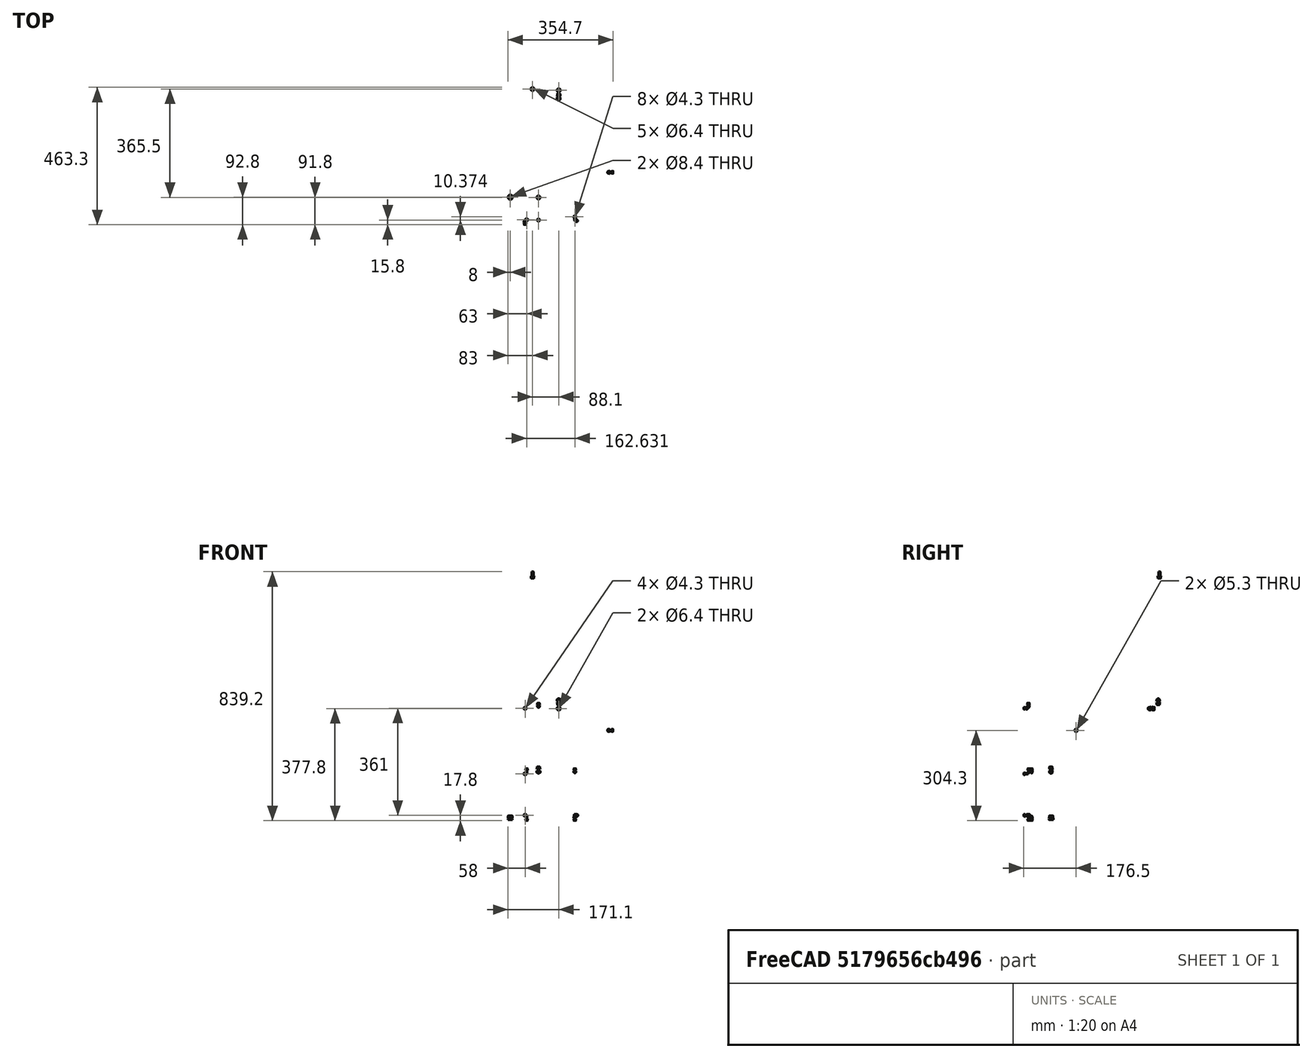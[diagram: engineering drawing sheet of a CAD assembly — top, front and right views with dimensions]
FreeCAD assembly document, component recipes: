
FREECAD ASSEMBLY — COMPONENT RECIPES ("OCT-FRAME-A")

This assembly document has 87 components, labeled P0..P86 below (a component is one placed body or linked part). 0 of them carry a construction recipe — the FreeCAD feature program that regenerates the part from scratch, quoted from this document or its linked companion documents; the rest are supplied as boundary geometry only. No exploded tour is included for this assembly.
COMPONENT P0 — geometry summary ("OCT-FRPLB-AA"; no construction recipe available for this part):
  bounding box: 422.0 x 422.0 x 3.0 mm
  tessellated surface: 3,756 triangles
  volume: 441062 mm^3 (83% of its bounding box)
  symmetry: 2-fold rotationally symmetric about the x axis; 2-fold rotationally symmetric about the y axis; 4-fold rotationally symmetric about the z axis; mirror-symmetric across its x mid-plane, y mid-plane, z mid-plane
COMPONENT P1 — geometry summary ("OCT-FRPLC-AA"; no construction recipe available for this part):
  bounding box: 422.0 x 422.0 x 3.0 mm
  tessellated surface: 8,208 triangles
  volume: 428125 mm^3 (80% of its bounding box)
COMPONENT P2 — geometry summary ("OCT-CPBRC-BA"; no construction recipe available for this part):
  bounding box: 170.0 x 20.0 x 20.0 mm
  tessellated surface: 804 triangles
  volume: 6888 mm^3 (10% of its bounding box)
  symmetry: mirror-symmetric across its x mid-plane
COMPONENT P3 — geometry summary ("OCT-LFPNL-AB"; no construction recipe available for this part):
  bounding box: 140.0 x 125.0 x 125.0 mm
  tessellated surface: 700 triangles
  volume: 48735 mm^3 (2% of its bounding box)
  symmetry: 2-fold rotationally symmetric about the z axis; mirror-symmetric across its z mid-plane
COMPONENT P4 — geometry summary ("OCT-LFPNL-AB"; no construction recipe available for this part):
  bounding box: 174.8 x 140.0 x 2.0 mm
  tessellated surface: 700 triangles
  volume: 48735 mm^3 (100% of its bounding box)
  symmetry: 2-fold rotationally symmetric about the x axis; 2-fold rotationally symmetric about the y axis; 2-fold rotationally symmetric about the z axis; mirror-symmetric across its x mid-plane, z mid-plane
COMPONENT P5 — geometry summary ("OCT-LFPNL-AB"; no construction recipe available for this part):
  bounding box: 140.0 x 125.0 x 125.0 mm
  tessellated surface: 700 triangles
  volume: 48735 mm^3 (2% of its bounding box)
  symmetry: 2-fold rotationally symmetric about the z axis; mirror-symmetric across its z mid-plane
COMPONENT P6 — geometry summary ("OCT-LFPNL-AB"; no construction recipe available for this part):
  bounding box: 140.0 x 125.0 x 125.0 mm
  tessellated surface: 700 triangles
  volume: 48735 mm^3 (2% of its bounding box)
  symmetry: 2-fold rotationally symmetric about the z axis; mirror-symmetric across its z mid-plane
COMPONENT P7 — geometry summary ("OCT-LFPNL-AB"; no construction recipe available for this part):
  bounding box: 174.8 x 140.0 x 2.0 mm
  tessellated surface: 700 triangles
  volume: 48735 mm^3 (100% of its bounding box)
  symmetry: 2-fold rotationally symmetric about the x axis; 2-fold rotationally symmetric about the y axis; 2-fold rotationally symmetric about the z axis; mirror-symmetric across its x mid-plane, z mid-plane
COMPONENT P8 — geometry summary ("OCT-LFPNL-AB"; no construction recipe available for this part):
  bounding box: 140.0 x 125.0 x 125.0 mm
  tessellated surface: 700 triangles
  volume: 48735 mm^3 (2% of its bounding box)
  symmetry: 2-fold rotationally symmetric about the z axis; mirror-symmetric across its z mid-plane
COMPONENT P9 — geometry summary ("OCT-LFPNL-BA"; no construction recipe available for this part):
  bounding box: 174.8 x 140.0 x 2.0 mm
  tessellated surface: 1,360 triangles
  volume: 29007 mm^3 (59% of its bounding box)
  symmetry: 2-fold rotationally symmetric about the x axis; 2-fold rotationally symmetric about the y axis; mirror-symmetric across its x mid-plane, y mid-plane
COMPONENT P10 — geometry summary ("OCT-LFPNL-CA"; no construction recipe available for this part):
  bounding box: 174.8 x 140.0 x 2.0 mm
  tessellated surface: 1,664 triangles
  volume: 27031 mm^3 (55% of its bounding box)
  symmetry: mirror-symmetric across its y mid-plane
COMPONENT P11 — geometry summary ("OCT-UFPNL-BB"; no construction recipe available for this part):
  bounding box: 241.0 x 174.8 x 1.5 mm
  tessellated surface: 1,580 triangles
  volume: 62827 mm^3 (99% of its bounding box)
  symmetry: 2-fold rotationally symmetric about the x axis; 2-fold rotationally symmetric about the y axis; 2-fold rotationally symmetric about the z axis; mirror-symmetric across its x mid-plane, y mid-plane, z mid-plane
COMPONENT P12 — geometry summary ("OCT-UFPNL-CB"; no construction recipe available for this part):
  bounding box: 241.0 x 174.8 x 1.5 mm
  tessellated surface: 1,324 triangles
  volume: 62936 mm^3 (100% of its bounding box)
  symmetry: 2-fold rotationally symmetric about the x axis; 2-fold rotationally symmetric about the y axis; 2-fold rotationally symmetric about the z axis; mirror-symmetric across its x mid-plane, y mid-plane, z mid-plane
COMPONENT P13 — geometry summary ("OCT-UFPNL-CB"; no construction recipe available for this part):
  bounding box: 241.0 x 174.8 x 1.5 mm
  tessellated surface: 1,324 triangles
  volume: 62936 mm^3 (100% of its bounding box)
  symmetry: 2-fold rotationally symmetric about the x axis; 2-fold rotationally symmetric about the y axis; 2-fold rotationally symmetric about the z axis; mirror-symmetric across its x mid-plane, y mid-plane, z mid-plane
COMPONENT P14 — geometry summary ("WDS4213-601"; no construction recipe available for this part):
  bounding box: 110.0 x 79.4 x 15.4 mm
  tessellated surface: 75,042 triangles
  volume: 34211 mm^3 (25% of its bounding box)
  symmetry: mirror-symmetric across its y mid-plane
COMPONENT P15 — geometry summary ("WDS4213-601"; no construction recipe available for this part):
  bounding box: 110.0 x 79.4 x 15.4 mm
  tessellated surface: 75,042 triangles
  volume: 34211 mm^3 (25% of its bounding box)
  symmetry: mirror-symmetric across its y mid-plane
COMPONENT P16 — geometry summary ("WDS673-82225"; no construction recipe available for this part):
  bounding box: 45.3 x 40.0 x 40.0 mm
  tessellated surface: 20,496 triangles
  volume: 12551 mm^3 (17% of its bounding box)
  symmetry: revolution-symmetric about the z axis through its bounding-box center; mirror-symmetric across its x mid-plane, y mid-plane
COMPONENT P17 — geometry summary ("WDS673-82225"; no construction recipe available for this part):
  bounding box: 45.3 x 40.0 x 40.0 mm
  tessellated surface: 20,496 triangles
  volume: 12551 mm^3 (17% of its bounding box)
  symmetry: revolution-symmetric about the z axis through its bounding-box center; mirror-symmetric across its x mid-plane, y mid-plane
COMPONENT P18 — geometry summary ("WDS673-82225"; no construction recipe available for this part):
  bounding box: 45.3 x 40.0 x 40.0 mm
  tessellated surface: 20,496 triangles
  volume: 12551 mm^3 (17% of its bounding box)
  symmetry: revolution-symmetric about the z axis through its bounding-box center; mirror-symmetric across its x mid-plane, y mid-plane
COMPONENT P19 — geometry summary ("WDS673-82225"; no construction recipe available for this part):
  bounding box: 45.3 x 40.0 x 40.0 mm
  tessellated surface: 20,496 triangles
  volume: 12551 mm^3 (17% of its bounding box)
  symmetry: revolution-symmetric about the z axis through its bounding-box center; mirror-symmetric across its x mid-plane, y mid-plane
COMPONENT P20 — geometry summary ("WDS8520-251"; no construction recipe available for this part):
  bounding box: 113.0 x 50.0 x 20.0 mm
  tessellated surface: 14,568 triangles
  volume: 33965 mm^3 (30% of its bounding box)
  symmetry: mirror-symmetric across its x mid-plane, y mid-plane
COMPONENT P21 — geometry summary ("637DSS"; no construction recipe available for this part):
  bounding box: 102.0 x 52.0 x 1.2 mm
  tessellated surface: 1,244 triangles
  volume: 6170 mm^3 (97% of its bounding box)
  symmetry: 2-fold rotationally symmetric about the x axis; 2-fold rotationally symmetric about the y axis; mirror-symmetric across its y mid-plane, z mid-plane
COMPONENT P22 — geometry summary ("637DSS"; no construction recipe available for this part):
  bounding box: 102.0 x 52.0 x 1.2 mm
  tessellated surface: 1,244 triangles
  volume: 6170 mm^3 (97% of its bounding box)
  symmetry: 2-fold rotationally symmetric about the x axis; 2-fold rotationally symmetric about the y axis; mirror-symmetric across its y mid-plane, z mid-plane
COMPONENT P23 — geometry summary ("baseplate block fasteners"; no construction recipe available for this part):
  bounding box: 411.0 x 149.0 x 16.0 mm
  tessellated surface: 8,512 triangles
  volume: 1289 mm^3 (0% of its bounding box)
  symmetry: 2-fold rotationally symmetric about the z axis; mirror-symmetric across its x mid-plane, y mid-plane
COMPONENT P24 — geometry summary ("baseplate bracket fasteners"; no construction recipe available for this part):
  bounding box: 412.4 x 394.3 x 16.0 mm
  tessellated surface: 83,040 triangles
  volume: 11254 mm^3 (0% of its bounding box)
  symmetry: 2-fold rotationally symmetric about the x axis; 2-fold rotationally symmetric about the y axis; 2-fold rotationally symmetric about the z axis; mirror-symmetric across its x mid-plane, y mid-plane, z mid-plane
COMPONENT P25 — geometry summary ("OCT-CHBRA-AC"; no construction recipe available for this part):
  bounding box: 80.0 x 25.0 x 25.0 mm
  tessellated surface: 600 triangles
  volume: 11180 mm^3 (22% of its bounding box)
  symmetry: mirror-symmetric across its x mid-plane
COMPONENT P26 — geometry summary ("OCT-CHBRA-AC"; no construction recipe available for this part):
  bounding box: 74.2 x 74.2 x 25.0 mm
  tessellated surface: 600 triangles
  volume: 11180 mm^3 (8% of its bounding box)
COMPONENT P27 — geometry summary ("OCT-CHBRA-AC"; no construction recipe available for this part):
  bounding box: 80.0 x 25.0 x 25.0 mm
  tessellated surface: 600 triangles
  volume: 11180 mm^3 (22% of its bounding box)
  symmetry: mirror-symmetric across its x mid-plane
COMPONENT P28 — geometry summary ("OCT-CHBRA-AC"; no construction recipe available for this part):
  bounding box: 74.2 x 74.2 x 25.0 mm
  tessellated surface: 600 triangles
  volume: 11180 mm^3 (8% of its bounding box)
COMPONENT P29 — geometry summary ("OCT-CHBRA-AC"; no construction recipe available for this part):
  bounding box: 80.0 x 25.0 x 25.0 mm
  tessellated surface: 600 triangles
  volume: 11180 mm^3 (22% of its bounding box)
  symmetry: mirror-symmetric across its x mid-plane
COMPONENT P30 — geometry summary ("OCT-CHBRA-AC"; no construction recipe available for this part):
  bounding box: 74.2 x 74.2 x 25.0 mm
  tessellated surface: 600 triangles
  volume: 11180 mm^3 (8% of its bounding box)
COMPONENT P31 — geometry summary ("OCT-CHBRA-AC"; no construction recipe available for this part):
  bounding box: 80.0 x 25.0 x 25.0 mm
  tessellated surface: 600 triangles
  volume: 11180 mm^3 (22% of its bounding box)
  symmetry: mirror-symmetric across its x mid-plane
COMPONENT P32 — geometry summary ("OCT-CHBRA-AC"; no construction recipe available for this part):
  bounding box: 74.2 x 74.2 x 25.0 mm
  tessellated surface: 600 triangles
  volume: 11180 mm^3 (8% of its bounding box)
COMPONENT P33 — geometry summary ("OCT-LBRAC-AA"; no construction recipe available for this part):
  bounding box: 123.3 x 123.3 x 20.0 mm
  tessellated surface: 620 triangles
  volume: 9368 mm^3 (3% of its bounding box)
COMPONENT P34 — geometry summary ("OCT-LBRAC-AA"; no construction recipe available for this part):
  bounding box: 170.0 x 20.0 x 20.0 mm
  tessellated surface: 620 triangles
  volume: 9368 mm^3 (14% of its bounding box)
  symmetry: mirror-symmetric across its y mid-plane
COMPONENT P35 — geometry summary ("OCT-LBRAC-AA"; no construction recipe available for this part):
  bounding box: 123.3 x 123.3 x 20.0 mm
  tessellated surface: 620 triangles
  volume: 9368 mm^3 (3% of its bounding box)
COMPONENT P36 — geometry summary ("OCT-LBRAC-AA"; no construction recipe available for this part):
  bounding box: 123.3 x 123.3 x 20.0 mm
  tessellated surface: 620 triangles
  volume: 9368 mm^3 (3% of its bounding box)
COMPONENT P37 — geometry summary ("OCT-LBRAC-AA"; no construction recipe available for this part):
  bounding box: 170.0 x 20.0 x 20.0 mm
  tessellated surface: 620 triangles
  volume: 9368 mm^3 (14% of its bounding box)
  symmetry: mirror-symmetric across its y mid-plane
COMPONENT P38 — geometry summary ("OCT-LBRAC-AA"; no construction recipe available for this part):
  bounding box: 123.3 x 123.3 x 20.0 mm
  tessellated surface: 620 triangles
  volume: 9368 mm^3 (3% of its bounding box)
COMPONENT P39 — geometry summary ("OCT-UBRAC-AA"; no construction recipe available for this part):
  bounding box: 123.3 x 123.3 x 40.0 mm
  tessellated surface: 916 triangles
  volume: 14427 mm^3 (2% of its bounding box)
COMPONENT P40 — geometry summary ("OCT-UBRAC-AA"; no construction recipe available for this part):
  bounding box: 170.0 x 40.0 x 20.0 mm
  tessellated surface: 916 triangles
  volume: 14427 mm^3 (11% of its bounding box)
  symmetry: mirror-symmetric across its y mid-plane
COMPONENT P41 — geometry summary ("OCT-UBRAC-AA"; no construction recipe available for this part):
  bounding box: 123.3 x 123.3 x 40.0 mm
  tessellated surface: 916 triangles
  volume: 14427 mm^3 (2% of its bounding box)
COMPONENT P42 — geometry summary ("OCT-UBRAC-AA"; no construction recipe available for this part):
  bounding box: 123.3 x 123.3 x 40.0 mm
  tessellated surface: 916 triangles
  volume: 14427 mm^3 (2% of its bounding box)
COMPONENT P43 — geometry summary ("OCT-UBRAC-AA"; no construction recipe available for this part):
  bounding box: 170.0 x 40.0 x 20.0 mm
  tessellated surface: 916 triangles
  volume: 14427 mm^3 (11% of its bounding box)
  symmetry: mirror-symmetric across its y mid-plane
COMPONENT P44 — geometry summary ("OCT-UBRAC-AA"; no construction recipe available for this part):
  bounding box: 123.3 x 123.3 x 40.0 mm
  tessellated surface: 916 triangles
  volume: 14427 mm^3 (2% of its bounding box)
COMPONENT P45 — geometry summary ("chamber brace fasteners"; no construction recipe available for this part):
  bounding box: 264.0 x 264.0 x 22.0 mm
  tessellated surface: 85,888 triangles
  volume: 23040 mm^3 (2% of its bounding box)
  symmetry: 2-fold rotationally symmetric about the x axis; 2-fold rotationally symmetric about the y axis; 4-fold rotationally symmetric about the z axis; mirror-symmetric across its x mid-plane, y mid-plane, z mid-plane
COMPONENT P46 — geometry summary ("OCT-CPBRC-AA"; no construction recipe available for this part):
  bounding box: 170.0 x 20.0 x 20.0 mm
  tessellated surface: 620 triangles
  volume: 9369 mm^3 (14% of its bounding box)
COMPONENT P47 — geometry summary ("OCT-CPBRC-AA"; no construction recipe available for this part):
  bounding box: 123.3 x 123.3 x 20.0 mm
  tessellated surface: 620 triangles
  volume: 9369 mm^3 (3% of its bounding box)
COMPONENT P48 — geometry summary ("OCT-CPBRC-AA"; no construction recipe available for this part):
  bounding box: 170.0 x 20.0 x 20.0 mm
  tessellated surface: 620 triangles
  volume: 9369 mm^3 (14% of its bounding box)
COMPONENT P49 — geometry summary ("OCT-CPBRC-AA"; no construction recipe available for this part):
  bounding box: 123.3 x 123.3 x 20.0 mm
  tessellated surface: 620 triangles
  volume: 9369 mm^3 (3% of its bounding box)
COMPONENT P50 — geometry summary ("OCT-CPBRC-AA"; no construction recipe available for this part):
  bounding box: 123.3 x 123.3 x 20.0 mm
  tessellated surface: 620 triangles
  volume: 9369 mm^3 (3% of its bounding box)
COMPONENT P51 — geometry summary ("OCT-CPBRC-AA"; no construction recipe available for this part):
  bounding box: 170.0 x 20.0 x 20.0 mm
  tessellated surface: 620 triangles
  volume: 9369 mm^3 (14% of its bounding box)
COMPONENT P52 — geometry summary ("OCT-CPBRC-AA"; no construction recipe available for this part):
  bounding box: 123.3 x 123.3 x 20.0 mm
  tessellated surface: 620 triangles
  volume: 9369 mm^3 (3% of its bounding box)
COMPONENT P53 — geometry summary ("foot fasteners"; no construction recipe available for this part):
  bounding box: 266.0 x 266.0 x 13.0 mm
  tessellated surface: 13,280 triangles
  volume: 4860 mm^3 (1% of its bounding box)
  symmetry: 2-fold rotationally symmetric about the x axis; 2-fold rotationally symmetric about the y axis; 4-fold rotationally symmetric about the z axis; mirror-symmetric across its x mid-plane, y mid-plane, z mid-plane
COMPONENT P54 — geometry summary ("hinge lower fastener set"; no construction recipe available for this part):
  bounding box: 22.0 x 12.0 x 12.0 mm
  tessellated surface: 5,368 triangles
  volume: 1440 mm^3 (45% of its bounding box)
  symmetry: 6-fold rotationally symmetric about the y axis; mirror-symmetric across its x mid-plane, z mid-plane
COMPONENT P55 — geometry summary ("hinge lower fastener set"; no construction recipe available for this part):
  bounding box: 22.0 x 12.0 x 12.0 mm
  tessellated surface: 5,368 triangles
  volume: 1440 mm^3 (45% of its bounding box)
  symmetry: 6-fold rotationally symmetric about the y axis; mirror-symmetric across its x mid-plane, z mid-plane
COMPONENT P56 — geometry summary ("hinge lower fastener set"; no construction recipe available for this part):
  bounding box: 22.0 x 12.0 x 12.0 mm
  tessellated surface: 5,368 triangles
  volume: 1440 mm^3 (45% of its bounding box)
  symmetry: 6-fold rotationally symmetric about the y axis; mirror-symmetric across its x mid-plane, z mid-plane
COMPONENT P57 — geometry summary ("hinge lower fastener set"; no construction recipe available for this part):
  bounding box: 22.0 x 12.0 x 12.0 mm
  tessellated surface: 5,368 triangles
  volume: 1440 mm^3 (45% of its bounding box)
  symmetry: 6-fold rotationally symmetric about the y axis; mirror-symmetric across its x mid-plane, z mid-plane
COMPONENT P58 — geometry summary ("hinge upper fasteners"; no construction recipe available for this part):
  bounding box: 22.0 x 12.0 x 12.0 mm
  tessellated surface: 5,368 triangles
  volume: 1440 mm^3 (45% of its bounding box)
  symmetry: 6-fold rotationally symmetric about the z axis
COMPONENT P59 — geometry summary ("hinge upper fasteners"; no construction recipe available for this part):
  bounding box: 22.0 x 12.0 x 12.0 mm
  tessellated surface: 5,368 triangles
  volume: 1440 mm^3 (45% of its bounding box)
  symmetry: 6-fold rotationally symmetric about the z axis
COMPONENT P60 — geometry summary ("hinge upper fasteners"; no construction recipe available for this part):
  bounding box: 22.0 x 12.0 x 12.0 mm
  tessellated surface: 5,368 triangles
  volume: 1440 mm^3 (45% of its bounding box)
  symmetry: 6-fold rotationally symmetric about the z axis
COMPONENT P61 — geometry summary ("hinge upper fasteners"; no construction recipe available for this part):
  bounding box: 22.0 x 12.0 x 12.0 mm
  tessellated surface: 5,368 triangles
  volume: 1440 mm^3 (45% of its bounding box)
  symmetry: 6-fold rotationally symmetric about the z axis
COMPONENT P62 — geometry summary ("lid frame"; no construction recipe available for this part):
  bounding box: 426.0 x 426.0 x 78.0 mm
  tessellated surface: 3,992 triangles
  volume: 504699 mm^3 (4% of its bounding box)
  symmetry: mirror-symmetric across its x mid-plane
COMPONENT P63 — geometry summary ("lid handle fastener group"; no construction recipe available for this part):
  bounding box: 22.0 x 12.0 x 12.0 mm
  tessellated surface: 3,352 triangles
  volume: 964 mm^3 (30% of its bounding box)
  symmetry: revolution-symmetric about the z axis through its bounding-box center
COMPONENT P64 — geometry summary ("lid handle fastener group"; no construction recipe available for this part):
  bounding box: 22.0 x 12.0 x 12.0 mm
  tessellated surface: 3,352 triangles
  volume: 964 mm^3 (30% of its bounding box)
  symmetry: revolution-symmetric about the z axis through its bounding-box center
COMPONENT P65 — geometry summary ("lifting handle fasteners"; no construction recipe available for this part):
  bounding box: 443.4 x 92.6 x 46.5 mm
  tessellated surface: 35,088 triangles
  volume: 6545 mm^3 (0% of its bounding box)
  symmetry: 2-fold rotationally symmetric about the z axis; mirror-symmetric across its x mid-plane, y mid-plane
COMPONENT P66 — geometry summary ("OCT-LBLOK-AB"; no construction recipe available for this part):
  bounding box: 20.0 x 20.0 x 20.0 mm
  tessellated surface: 410 triangles
  volume: 7741 mm^3 (97% of its bounding box)
  symmetry: mirror-symmetric across its z mid-plane
COMPONENT P67 — geometry summary ("OCT-LBLOK-AB"; no construction recipe available for this part):
  bounding box: 20.0 x 20.0 x 20.0 mm
  tessellated surface: 410 triangles
  volume: 7741 mm^3 (97% of its bounding box)
  symmetry: mirror-symmetric across its z mid-plane
COMPONENT P68 — geometry summary ("OCT-LBLOK-AB"; no construction recipe available for this part):
  bounding box: 20.0 x 20.0 x 20.0 mm
  tessellated surface: 410 triangles
  volume: 7741 mm^3 (97% of its bounding box)
  symmetry: mirror-symmetric across its z mid-plane
COMPONENT P69 — geometry summary ("OCT-LBLOK-AB"; no construction recipe available for this part):
  bounding box: 20.0 x 20.0 x 20.0 mm
  tessellated surface: 410 triangles
  volume: 7741 mm^3 (97% of its bounding box)
  symmetry: mirror-symmetric across its z mid-plane
COMPONENT P70 — geometry summary ("lower panel block fasteners"; no construction recipe available for this part):
  bounding box: 435.6 x 159.0 x 129.0 mm
  tessellated surface: 17,024 triangles
  volume: 2377 mm^3 (0% of its bounding box)
  symmetry: 2-fold rotationally symmetric about the x axis; 2-fold rotationally symmetric about the y axis; 2-fold rotationally symmetric about the z axis; mirror-symmetric across its x mid-plane, y mid-plane, z mid-plane
COMPONENT P71 — geometry summary ("lower panel bracket fasteners"; no construction recipe available for this part):
  bounding box: 435.6 x 418.7 x 129.0 mm
  tessellated surface: 83,040 triangles
  volume: 10651 mm^3 (0% of its bounding box)
  symmetry: 2-fold rotationally symmetric about the x axis; 2-fold rotationally symmetric about the y axis; 2-fold rotationally symmetric about the z axis; mirror-symmetric across its x mid-plane, y mid-plane, z mid-plane
COMPONENT P72 — geometry summary ("mid plate block fasteners"; no construction recipe available for this part):
  bounding box: 411.0 x 149.0 x 16.0 mm
  tessellated surface: 8,512 triangles
  volume: 1289 mm^3 (0% of its bounding box)
  symmetry: 2-fold rotationally symmetric about the z axis; mirror-symmetric across its x mid-plane, y mid-plane
COMPONENT P73 — geometry summary ("mid plate bracket fasteners"; no construction recipe available for this part):
  bounding box: 411.0 x 392.3 x 16.0 mm
  tessellated surface: 41,520 triangles
  volume: 5627 mm^3 (0% of its bounding box)
  symmetry: 2-fold rotationally symmetric about the x axis; 2-fold rotationally symmetric about the y axis; 2-fold rotationally symmetric about the z axis; mirror-symmetric across its x mid-plane, y mid-plane, z mid-plane
COMPONENT P74 — geometry summary ("OCT-CHTOP-AA"; no construction recipe available for this part):
  bounding box: 422.0 x 422.0 x 3.0 mm
  tessellated surface: 5,952 triangles
  volume: 228384 mm^3 (43% of its bounding box)
  symmetry: 2-fold rotationally symmetric about the x axis; 2-fold rotationally symmetric about the y axis; 4-fold rotationally symmetric about the z axis; mirror-symmetric across its x mid-plane, y mid-plane, z mid-plane
COMPONENT P75 — geometry summary ("top plate fasteners"; no construction recipe available for this part):
  bounding box: 413.0 x 413.0 x 16.0 mm
  tessellated surface: 55,360 triangles
  volume: 7503 mm^3 (0% of its bounding box)
  symmetry: 2-fold rotationally symmetric about the x axis; 2-fold rotationally symmetric about the y axis; 4-fold rotationally symmetric about the z axis; mirror-symmetric across its x mid-plane, y mid-plane, z mid-plane
COMPONENT P76 — geometry summary ("OCT-ULBLK-AB"; no construction recipe available for this part):
  bounding box: 40.0 x 20.0 x 20.0 mm
  tessellated surface: 858 triangles
  volume: 15786 mm^3 (99% of its bounding box)
COMPONENT P77 — geometry summary ("OCT-ULBLK-AB"; no construction recipe available for this part):
  bounding box: 40.0 x 20.0 x 20.0 mm
  tessellated surface: 858 triangles
  volume: 15786 mm^3 (99% of its bounding box)
COMPONENT P78 — geometry summary ("OCT-UFPNL-AB"; no construction recipe available for this part):
  bounding box: 241.0 x 174.8 x 1.5 mm
  tessellated surface: 620 triangles
  volume: 63058 mm^3 (100% of its bounding box)
  symmetry: 2-fold rotationally symmetric about the x axis; 2-fold rotationally symmetric about the y axis; 2-fold rotationally symmetric about the z axis; mirror-symmetric across its x mid-plane, y mid-plane, z mid-plane
COMPONENT P79 — geometry summary ("OCT-UFPNL-AB"; no construction recipe available for this part):
  bounding box: 241.0 x 124.7 x 124.7 mm
  tessellated surface: 620 triangles
  volume: 63058 mm^3 (2% of its bounding box)
  symmetry: 2-fold rotationally symmetric about the z axis; mirror-symmetric across its z mid-plane
COMPONENT P80 — geometry summary ("OCT-UFPNL-AB"; no construction recipe available for this part):
  bounding box: 241.0 x 124.7 x 124.7 mm
  tessellated surface: 620 triangles
  volume: 63058 mm^3 (2% of its bounding box)
  symmetry: 2-fold rotationally symmetric about the z axis; mirror-symmetric across its z mid-plane
COMPONENT P81 — geometry summary ("OCT-UFPNL-AB"; no construction recipe available for this part):
  bounding box: 241.0 x 124.7 x 124.7 mm
  tessellated surface: 620 triangles
  volume: 63058 mm^3 (2% of its bounding box)
  symmetry: 2-fold rotationally symmetric about the z axis; mirror-symmetric across its z mid-plane
COMPONENT P82 — geometry summary ("OCT-UFPNL-AB"; no construction recipe available for this part):
  bounding box: 241.0 x 124.7 x 124.7 mm
  tessellated surface: 620 triangles
  volume: 63058 mm^3 (2% of its bounding box)
  symmetry: 2-fold rotationally symmetric about the z axis; mirror-symmetric across its z mid-plane
COMPONENT P83 — geometry summary ("upper panel block fasteners"; no construction recipe available for this part):
  bounding box: 434.6 x 159.0 x 9.0 mm
  tessellated surface: 8,512 triangles
  volume: 1188 mm^3 (0% of its bounding box)
  symmetry: 2-fold rotationally symmetric about the x axis; 2-fold rotationally symmetric about the y axis; 2-fold rotationally symmetric about the z axis; mirror-symmetric across its x mid-plane, y mid-plane, z mid-plane
COMPONENT P84 — geometry summary ("upper panel bracket fasteners"; no construction recipe available for this part):
  bounding box: 434.6 x 434.6 x 230.0 mm
  tessellated surface: 96,880 triangles
  volume: 12426 mm^3 (0% of its bounding box)
  symmetry: 2-fold rotationally symmetric about the z axis; mirror-symmetric across its x mid-plane, y mid-plane
COMPONENT P85 — geometry summary ("OCT-URBLK-AB"; no construction recipe available for this part):
  bounding box: 40.0 x 20.0 x 20.0 mm
  tessellated surface: 858 triangles
  volume: 15718 mm^3 (98% of its bounding box)
COMPONENT P86 — geometry summary ("OCT-URBLK-AB"; no construction recipe available for this part):
  bounding box: 40.0 x 20.0 x 20.0 mm
  tessellated surface: 858 triangles
  volume: 15718 mm^3 (98% of its bounding box)
PROVENANCE & LICENSES
A FreeCAD (.FCStd) document from a public repository crawl; recipes are the document's own serialized feature recipes (and, for linked parts, companion documents' recipes).
License: mit.
